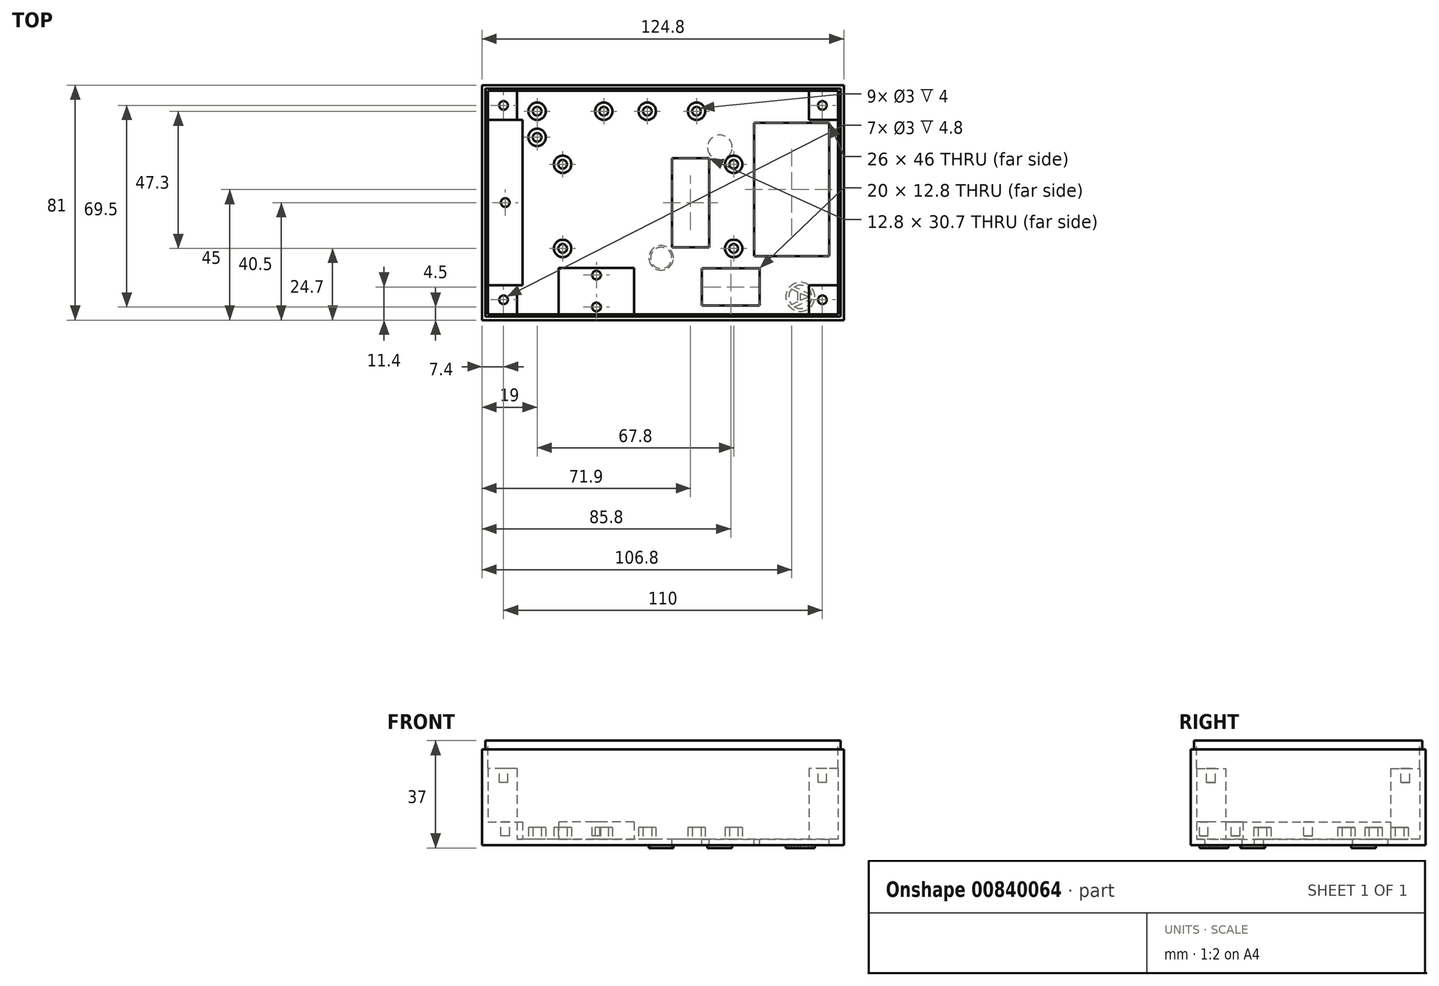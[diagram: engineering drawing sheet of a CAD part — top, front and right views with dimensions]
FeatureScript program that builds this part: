
annotation { "Feature Type Name" : "Feature", "Feature Type Description" : "" }
export const myFeature = defineFeature(function(context is Context, id is Id, definition is map)
    precondition{}
    {
        {
            var Q0;
            Q0=qCreatedBy(makeId("Top.planeOp"),FACE);
            var sketch = newSketch(context, id + "F0", { "sketchPlane" : qUnion([Q0])});
            skLineSegment(sketch, "E0.bottom", {"start": v(62.4, -40.5) * mm, "end": v(-62.4, -40.5) * mm});
            skLineSegment(sketch, "E0.top", {"start": v(62.4, 40.5) * mm, "end": v(-62.4, 40.5) * mm});
            skLineSegment(sketch, "E0.left", {"start": v(62.4, -40.5) * mm, "end": v(62.4, 40.5) * mm});
            skLineSegment(sketch, "E0.right", {"start": v(-62.4, -40.5) * mm, "end": v(-62.4, 40.5) * mm});
            skPoint(sketch, "E0.middle", {"position": v(0, 0) * mm});
            skSolve(sketch);
        }
        {
            var Q0;
            Q0=qSketchRegion(id+"F0",true);
            extrude(context, id + "F1", {"entities" : qUnion([Q0]), "depth" : 33 * mm, "offsetDistance" : 25 * mm});
        }
        {
            var Q0;
            Q0=makeQuery(id+"F1.opExtrude","CAP_FACE",FACE,{"disambiguationData":[OSD([sQuery(id+"F0.wireOp",EDGE,"E0.bottom"),sQuery(id+"F0.wireOp",EDGE,"E0.top"),sQuery(id+"F0.wireOp",EDGE,"E0.left"),sQuery(id+"F0.wireOp",EDGE,"E0.right")])],"isStart":false});
            var sketch = newSketch(context, id + "F2", { "sketchPlane" : qUnion([Q0])});
            skLineSegment(sketch, "E1.bottom", {"start": v(61.25, -39.35) * mm, "end": v(-61.25, -39.35) * mm});
            skLineSegment(sketch, "E1.top", {"start": v(61.25, 39.35) * mm, "end": v(-61.25, 39.35) * mm});
            skLineSegment(sketch, "E1.left", {"start": v(61.25, -39.35) * mm, "end": v(61.25, 39.35) * mm});
            skLineSegment(sketch, "E1.right", {"start": v(-61.25, -39.35) * mm, "end": v(-61.25, 39.35) * mm});
            skPoint(sketch, "E1.middle", {"position": v(0, 0) * mm});
            skSolve(sketch);
        }
        {
            var Q0;
            Q0=qSketchRegion(id+"F2",true);
            extrude(context, id + "F3", {"entities" : qUnion([Q0]), "operationType" : NewBodyOperationType.ADD, "depth" : 3 * mm, "offsetDistance" : 25 * mm});
        }
        {
            var Q0;
            Q0=makeQuery(id+"F3.opExtrude","CAP_FACE",FACE,{"disambiguationData":[OSD([sQuery(id+"F2.wireOp",EDGE,"E1.bottom"),sQuery(id+"F2.wireOp",EDGE,"E1.top"),sQuery(id+"F2.wireOp",EDGE,"E1.left"),sQuery(id+"F2.wireOp",EDGE,"E1.right")])],"isStart":false});
            var sketch = newSketch(context, id + "F4", { "sketchPlane" : qUnion([Q0])});
            skLineSegment(sketch, "E2.bottom", {"start": v(60.4, -38.5) * mm, "end": v(-60.4, -38.5) * mm});
            skLineSegment(sketch, "E2.top", {"start": v(60.4, 38.5) * mm, "end": v(-60.4, 38.5) * mm});
            skLineSegment(sketch, "E2.left", {"start": v(60.4, -38.5) * mm, "end": v(60.4, 38.5) * mm});
            skLineSegment(sketch, "E2.right", {"start": v(-60.4, -38.5) * mm, "end": v(-60.4, 38.5) * mm});
            skPoint(sketch, "E2.middle", {"position": v(0, 0) * mm});
            skSolve(sketch);
        }
        {
            var Q0;
            Q0=qSketchRegion(id+"F4",true);
            extrude(context, id + "F5", {"entities" : qUnion([Q0]), "operationType" : NewBodyOperationType.REMOVE, "oppositeDirection" : true, "depth" : 34 * mm, "offsetDistance" : 25 * mm});
        }
        {
            var Q0;
            Q0=makeQuery(id+"F5.boolean.opBoolean","COPY",FACE,{"derivedFrom":makeQuery(id+"F5.opExtrude","CAP_FACE",FACE,{"disambiguationData":[OSD([sQuery(id+"F4.wireOp",EDGE,"E2.bottom"),sQuery(id+"F4.wireOp",EDGE,"E2.top"),sQuery(id+"F4.wireOp",EDGE,"E2.left"),sQuery(id+"F4.wireOp",EDGE,"E2.right")])],"isStart":false})});
            var sketch = newSketch(context, id + "F6", { "sketchPlane" : qUnion([Q0])});
            skLineSegment(sketch, "E3.bottom", {"start": v(-60.4, 38.5) * mm, "end": v(-50.4, 38.5) * mm});
            skLineSegment(sketch, "E3.top", {"start": v(-60.4, 28.5) * mm, "end": v(-50.4, 28.5) * mm});
            skLineSegment(sketch, "E3.left", {"start": v(-60.4, 38.5) * mm, "end": v(-60.4, 28.5) * mm});
            skLineSegment(sketch, "E3.right", {"start": v(-50.4, 38.5) * mm, "end": v(-50.4, 28.5) * mm});
            skLineSegment(sketch, "E4.bottom", {"start": v(-60.4, -38.5) * mm, "end": v(-50.4, -38.5) * mm});
            skLineSegment(sketch, "E4.top", {"start": v(-60.4, -28.5) * mm, "end": v(-50.4, -28.5) * mm});
            skLineSegment(sketch, "E4.left", {"start": v(-60.4, -38.5) * mm, "end": v(-60.4, -28.5) * mm});
            skLineSegment(sketch, "E4.right", {"start": v(-50.4, -38.5) * mm, "end": v(-50.4, -28.5) * mm});
            skLineSegment(sketch, "E5.bottom", {"start": v(60.4, -38.5) * mm, "end": v(50.4, -38.5) * mm});
            skLineSegment(sketch, "E5.top", {"start": v(60.4, -28.5) * mm, "end": v(50.4, -28.5) * mm});
            skLineSegment(sketch, "E5.left", {"start": v(60.4, -38.5) * mm, "end": v(60.4, -28.5) * mm});
            skLineSegment(sketch, "E5.right", {"start": v(50.4, -38.5) * mm, "end": v(50.4, -28.5) * mm});
            skLineSegment(sketch, "E6.bottom", {"start": v(60.4, 38.5) * mm, "end": v(50.4, 38.5) * mm});
            skLineSegment(sketch, "E6.top", {"start": v(60.4, 28.5) * mm, "end": v(50.4, 28.5) * mm});
            skLineSegment(sketch, "E6.left", {"start": v(60.4, 38.5) * mm, "end": v(60.4, 28.5) * mm});
            skLineSegment(sketch, "E6.right", {"start": v(50.4, 38.5) * mm, "end": v(50.4, 28.5) * mm});
            skSolve(sketch);
        }
        {
            var Q0;
            Q0=qSketchRegion(id+"F6",true);
            extrude(context, id + "F7", {"entities" : qUnion([Q0]), "operationType" : NewBodyOperationType.ADD, "depth" : 24.4 * mm, "offsetDistance" : 25 * mm});
        }
        {
            var Q0;
            Q0=makeQuery(id+"F7.opExtrude","CAP_FACE",FACE,{"disambiguationData":[OSD([sQuery(id+"F6.wireOp",EDGE,"E3.bottom"),sQuery(id+"F6.wireOp",EDGE,"E3.top"),sQuery(id+"F6.wireOp",EDGE,"E3.left"),sQuery(id+"F6.wireOp",EDGE,"E3.right")])],"isStart":false});
            var sketch = newSketch(context, id + "F8", { "sketchPlane" : qUnion([Q0])});
            skCircle(sketch, "E7", {"center": v(-55, 33.5) * mm, "radius": 1.5 * mm});
            skPoint(sketch, "E7.centerSnap0", {"position": v(-50.4, 33.5) * mm});
            skCircle(sketch, "E8", {"center": v(-55, -33.5) * mm, "radius": 1.5 * mm});
            skCircle(sketch, "E9", {"center": v(55, -33.5) * mm, "radius": 1.5 * mm});
            skCircle(sketch, "E10", {"center": v(55, 33.5) * mm, "radius": 1.5 * mm});
            skSolve(sketch);
        }
        {
            var Q0;
            Q0=qSketchRegion(id+"F8",true);
            extrude(context, id + "F9", {"entities" : qUnion([Q0]), "operationType" : NewBodyOperationType.REMOVE, "oppositeDirection" : true, "depth" : 4.8 * mm, "offsetDistance" : 25 * mm});
        }
        {
            var Q0;
            Q0=makeQuery(id+"F5.boolean.opBoolean","COPY",FACE,{"derivedFrom":makeQuery(id+"F5.opExtrude","CAP_FACE",FACE,{"disambiguationData":[OSD([sQuery(id+"F4.wireOp",EDGE,"E2.bottom"),sQuery(id+"F4.wireOp",EDGE,"E2.top"),sQuery(id+"F4.wireOp",EDGE,"E2.left"),sQuery(id+"F4.wireOp",EDGE,"E2.right")])],"isStart":false})});
            var sketch = newSketch(context, id + "F10", { "sketchPlane" : qUnion([Q0])});
            skLineSegment(sketch, "E11.bottom", {"start": v(31.4, 27.5) * mm, "end": v(57.4, 27.5) * mm});
            skLineSegment(sketch, "E11.top", {"start": v(31.4, -18.5) * mm, "end": v(57.4, -18.5) * mm});
            skLineSegment(sketch, "E11.left", {"start": v(31.4, 27.5) * mm, "end": v(31.4, -18.5) * mm});
            skLineSegment(sketch, "E11.right", {"start": v(57.4, 27.5) * mm, "end": v(57.4, -18.5) * mm});
            skLineSegment(sketch, "E12.bottom", {"start": v(13.4, -22.7) * mm, "end": v(33.4, -22.7) * mm});
            skLineSegment(sketch, "E12.top", {"start": v(13.4, -35.5) * mm, "end": v(33.4, -35.5) * mm});
            skLineSegment(sketch, "E12.left", {"start": v(13.4, -22.7) * mm, "end": v(13.4, -35.5) * mm});
            skLineSegment(sketch, "E12.right", {"start": v(33.4, -22.7) * mm, "end": v(33.4, -35.5) * mm});
            skLineSegment(sketch, "E13.bottom", {"start": v(15.9, -15.35) * mm, "end": v(3.1, -15.35) * mm});
            skLineSegment(sketch, "E13.top", {"start": v(15.9, 15.35) * mm, "end": v(3.1, 15.35) * mm});
            skLineSegment(sketch, "E13.left", {"start": v(15.9, -15.35) * mm, "end": v(15.9, 15.35) * mm});
            skLineSegment(sketch, "E13.right", {"start": v(3.1, -15.35) * mm, "end": v(3.1, 15.35) * mm});
            skPoint(sketch, "E13.middle", {"position": v(9.5, 0) * mm});
            skSolve(sketch);
        }
        {
            var Q0;
            Q0=qSketchRegion(id+"F10",true);
            extrude(context, id + "F11", {"entities" : qUnion([Q0]), "operationType" : NewBodyOperationType.REMOVE, "endBound" : BoundingType.THROUGH_ALL, "oppositeDirection" : true, "depth" : 25 * mm, "offsetDistance" : 25 * mm});
        }
        {
            var Q0;
            Q0=makeQuery(id+"F5.boolean.opBoolean","COPY",FACE,{"derivedFrom":makeQuery(id+"F5.opExtrude","CAP_FACE",FACE,{"disambiguationData":[OSD([sQuery(id+"F4.wireOp",EDGE,"E2.bottom"),sQuery(id+"F4.wireOp",EDGE,"E2.top"),sQuery(id+"F4.wireOp",EDGE,"E2.left"),sQuery(id+"F4.wireOp",EDGE,"E2.right")])],"isStart":false})});
            var sketch = newSketch(context, id + "F12", { "sketchPlane" : qUnion([Q0])});
            skCircle(sketch, "E14", {"center": v(24.4, 13.2) * mm, "radius": 3 * mm});
            skCircle(sketch, "E15", {"center": v(-34.6, 13.2) * mm, "radius": 3 * mm});
            skCircle(sketch, "E16", {"center": v(-34.6, -15.8) * mm, "radius": 3 * mm});
            skCircle(sketch, "E17", {"center": v(24.4, -15.8) * mm, "radius": 3 * mm});
            skCircle(sketch, "E18", {"center": v(-43.4, 31.5) * mm, "radius": 3 * mm});
            skCircle(sketch, "E19", {"center": v(-43.4, 22.5) * mm, "radius": 3 * mm});
            skCircle(sketch, "E20", {"center": v(-20.4, 31.5) * mm, "radius": 3 * mm});
            skCircle(sketch, "E21", {"center": v(-5.4, 31.5) * mm, "radius": 3 * mm});
            skCircle(sketch, "E22", {"center": v(11.6, 31.5) * mm, "radius": 3 * mm});
            skSolve(sketch);
        }
        {
            var Q0;
            Q0=qSketchRegion(id+"F12",true);
            extrude(context, id + "F13", {"entities" : qUnion([Q0]), "operationType" : NewBodyOperationType.ADD, "depth" : 4 * mm, "offsetDistance" : 25 * mm});
        }
        {
            var Q0;
            Q0=makeQuery(id+"F5.boolean.opBoolean","COPY",FACE,{"derivedFrom":makeQuery(id+"F5.opExtrude","CAP_FACE",FACE,{"disambiguationData":[OSD([sQuery(id+"F4.wireOp",EDGE,"E2.bottom"),sQuery(id+"F4.wireOp",EDGE,"E2.top"),sQuery(id+"F4.wireOp",EDGE,"E2.left"),sQuery(id+"F4.wireOp",EDGE,"E2.right")])],"isStart":false})});
            var sketch = newSketch(context, id + "F14", { "sketchPlane" : qUnion([Q0])});
            skCircle(sketch, "E23", {"center": v(-34.6, -15.8) * mm, "radius": 1.5 * mm});
            skCircle(sketch, "E24", {"center": v(24.4, -15.8) * mm, "radius": 1.5 * mm});
            skCircle(sketch, "E25", {"center": v(-34.6, 13.2) * mm, "radius": 1.5 * mm});
            skCircle(sketch, "E26", {"center": v(24.4, 13.2) * mm, "radius": 1.5 * mm});
            skCircle(sketch, "E27", {"center": v(11.6, 31.5) * mm, "radius": 1.5 * mm});
            skCircle(sketch, "E28", {"center": v(-5.4, 31.5) * mm, "radius": 1.5 * mm});
            skCircle(sketch, "E29", {"center": v(-20.4, 31.5) * mm, "radius": 1.5 * mm});
            skCircle(sketch, "E30", {"center": v(-43.4, 22.5) * mm, "radius": 1.5 * mm});
            skCircle(sketch, "E31", {"center": v(-43.4, 31.5) * mm, "radius": 1.5 * mm});
            skSolve(sketch);
        }
        {
            var Q0;
            Q0=qSketchRegion(id+"F14",true);
            extrude(context, id + "F15", {"entities" : qUnion([Q0]), "operationType" : NewBodyOperationType.REMOVE, "depth" : 4.8 * mm, "offsetDistance" : 25 * mm});
        }
        {
            var Q0;
            Q0=makeQuery(id+"F5.boolean.opBoolean","COPY",FACE,{"derivedFrom":makeQuery(id+"F5.opExtrude","CAP_FACE",FACE,{"disambiguationData":[OSD([sQuery(id+"F4.wireOp",EDGE,"E2.bottom"),sQuery(id+"F4.wireOp",EDGE,"E2.top"),sQuery(id+"F4.wireOp",EDGE,"E2.left"),sQuery(id+"F4.wireOp",EDGE,"E2.right")])],"isStart":false})});
            var sketch = newSketch(context, id + "F16", { "sketchPlane" : qUnion([Q0])});
            skLineSegment(sketch, "E32.bottom", {"start": v(-60.4, -28.5) * mm, "end": v(-48.4, -28.5) * mm});
            skLineSegment(sketch, "E32.top", {"start": v(-60.4, 28.5) * mm, "end": v(-48.4, 28.5) * mm});
            skLineSegment(sketch, "E32.left", {"start": v(-60.4, -28.5) * mm, "end": v(-60.4, 28.5) * mm});
            skLineSegment(sketch, "E32.right", {"start": v(-48.4, -28.5) * mm, "end": v(-48.4, 28.5) * mm});
            skSolve(sketch);
        }
        {
            var Q0;
            Q0=qSketchRegion(id+"F16",true);
            extrude(context, id + "F17", {"entities" : qUnion([Q0]), "operationType" : NewBodyOperationType.ADD, "depth" : 6 * mm, "offsetDistance" : 25 * mm});
        }
        {
            var Q0;
            Q0=makeQuery(id+"F17.opExtrude","CAP_FACE",FACE,{"disambiguationData":[OSD([sQuery(id+"F16.wireOp",EDGE,"E32.bottom"),sQuery(id+"F16.wireOp",EDGE,"E32.top"),sQuery(id+"F16.wireOp",EDGE,"E32.left"),sQuery(id+"F16.wireOp",EDGE,"E32.right")])],"isStart":false});
            var sketch = newSketch(context, id + "F18", { "sketchPlane" : qUnion([Q0])});
            skCircle(sketch, "E33", {"center": v(-54.4, 0) * mm, "radius": 1.5 * mm});
            skPoint(sketch, "E33.centerSnap0", {"position": v(-48.4, 0) * mm});
            skSolve(sketch);
        }
        {
            var Q0;
            Q0=qSketchRegion(id+"F18",true);
            extrude(context, id + "F19", {"entities" : qUnion([Q0]), "operationType" : NewBodyOperationType.REMOVE, "oppositeDirection" : true, "depth" : 4.8 * mm, "offsetDistance" : 25 * mm});
        }
        {
            var Q0;
            Q0=makeQuery(id+"F5.boolean.opBoolean","COPY",FACE,{"derivedFrom":makeQuery(id+"F5.opExtrude","CAP_FACE",FACE,{"disambiguationData":[OSD([sQuery(id+"F4.wireOp",EDGE,"E2.bottom"),sQuery(id+"F4.wireOp",EDGE,"E2.top"),sQuery(id+"F4.wireOp",EDGE,"E2.left"),sQuery(id+"F4.wireOp",EDGE,"E2.right")])],"isStart":false})});
            var sketch = newSketch(context, id + "F20", { "sketchPlane" : qUnion([Q0])});
            skLineSegment(sketch, "E34.bottom", {"start": v(-35.93, -22.5) * mm, "end": v(-9.93, -22.5) * mm});
            skLineSegment(sketch, "E34.top", {"start": v(-35.93, -38.5) * mm, "end": v(-9.93, -38.5) * mm});
            skLineSegment(sketch, "E34.left", {"start": v(-35.93, -22.5) * mm, "end": v(-35.93, -38.5) * mm});
            skLineSegment(sketch, "E34.right", {"start": v(-9.93, -22.5) * mm, "end": v(-9.93, -38.5) * mm});
            skSolve(sketch);
        }
        {
            var Q0;
            Q0=qSketchRegion(id+"F20",true);
            extrude(context, id + "F21", {"entities" : qUnion([Q0]), "operationType" : NewBodyOperationType.ADD, "depth" : 6 * mm, "offsetDistance" : 25 * mm});
        }
        {
            var Q0;
            Q0=makeQuery(id+"F21.opExtrude","CAP_FACE",FACE,{"disambiguationData":[OSD([sQuery(id+"F20.wireOp",EDGE,"E34.bottom"),sQuery(id+"F20.wireOp",EDGE,"E34.top"),sQuery(id+"F20.wireOp",EDGE,"E34.left"),sQuery(id+"F20.wireOp",EDGE,"E34.right")])],"isStart":false});
            var sketch = newSketch(context, id + "F22", { "sketchPlane" : qUnion([Q0])});
            skCircle(sketch, "E35", {"center": v(-22.93, -25) * mm, "radius": 1.5 * mm});
            skPoint(sketch, "E35.centerSnap0", {"position": v(-22.93, -22.5) * mm});
            skPoint(sketch, "E35.perimeterSnap0", {"position": v(-22.93, -22.5) * mm});
            skPoint(sketch, "E35.perimeterSnap1", {"position": v(-35.93, -30.5) * mm});
            skCircle(sketch, "E36", {"center": v(-22.93, -36) * mm, "radius": 1.5 * mm});
            skSolve(sketch);
        }
        {
            var Q0;
            Q0=qSketchRegion(id+"F22",true);
            extrude(context, id + "F23", {"entities" : qUnion([Q0]), "operationType" : NewBodyOperationType.REMOVE, "oppositeDirection" : true, "depth" : 4.8 * mm, "offsetDistance" : 25 * mm});
        }
        {
            var Q0;
            Q0=makeQuery(id+"F1.opExtrude","CAP_FACE",FACE,{"disambiguationData":[OSD([sQuery(id+"F0.wireOp",EDGE,"E0.bottom"),sQuery(id+"F0.wireOp",EDGE,"E0.top"),sQuery(id+"F0.wireOp",EDGE,"E0.left"),sQuery(id+"F0.wireOp",EDGE,"E0.right")])],"isStart":true});
            var sketch = newSketch(context, id + "F24", { "sketchPlane" : qUnion([Q0])});
            skCircle(sketch, "E37", {"center": v(47.4, 32.5) * mm, "radius": 5 * mm});
            skCircle(sketch, "E38", {"center": v(47.4, 32.5) * mm, "radius": 4 * mm});
            skSolve(sketch);
        }
        {
            var Q0;
            Q0=qSketchRegion(id+"F24",true);
            extrude(context, id + "F25", {"entities" : qUnion([Q0]), "operationType" : NewBodyOperationType.ADD, "depth" : 1 * mm, "offsetDistance" : 25 * mm});
        }
        {
            var Q0;
            {var subQ12=sQuery(id+"F0.wireOp",EDGE,"E0.right");var subQ14=sQuery(id+"F0.wireOp",EDGE,"E0.top");var subQ16=sQuery(id+"F0.wireOp",EDGE,"E0.left");var subQ18=sQuery(id+"F0.wireOp",EDGE,"E0.bottom");var subQ19=makeQuery(id+"F1.opExtrude","SWEPT_FACE",FACE,{"disambiguationData":[OSD([subQ18])]});Q0=makeQuery(id+"FWEkfTlQKALJ9jg_1.boolean.opBoolean","SPLIT",FACE,{"disambiguationData":[TD([subQ19])],"derivedFrom":makeQuery(id+"F25.boolean.opBoolean","SPLIT",FACE,{"disambiguationData":[TD([subQ19])],"derivedFrom":makeQuery(id+"F1.opExtrude","CAP_FACE",FACE,{"disambiguationData":[OSD([subQ18,subQ14,subQ16,subQ12])],"isStart":true})})});}
            var sketch = newSketch(context, id + "F26", { "sketchPlane" : qUnion([Q0])});
            skLineSegment(sketch, "E39", {"start": v(44.91, 36.12) * mm, "end": v(51.52, 33.06) * mm});
            skLineSegment(sketch, "E40", {"start": v(51.52, 33.06) * mm, "end": v(51.52, 31.97) * mm});
            skLineSegment(sketch, "E41", {"start": v(51.52, 31.97) * mm, "end": v(45.1, 28.97) * mm});
            skLineSegment(sketch, "E42", {"start": v(45.1, 28.97) * mm, "end": v(44.19, 29.7) * mm});
            skLineSegment(sketch, "E43", {"start": v(44.19, 29.7) * mm, "end": v(46.4, 30.75) * mm});
            skLineSegment(sketch, "E44", {"start": v(46.4, 30.75) * mm, "end": v(46.4, 34.26) * mm});
            skLineSegment(sketch, "E45", {"start": v(46.4, 34.26) * mm, "end": v(44.17, 35.3) * mm});
            skLineSegment(sketch, "E46", {"start": v(44.17, 35.3) * mm, "end": v(44.91, 36.12) * mm});
            skLineSegment(sketch, "E47", {"start": v(50.23, 32.5) * mm, "end": v(47.48, 33.76) * mm});
            skLineSegment(sketch, "E48", {"start": v(47.48, 33.76) * mm, "end": v(47.48, 31.24) * mm});
            skLineSegment(sketch, "E49", {"start": v(47.48, 31.24) * mm, "end": v(50.23, 32.5) * mm});
            skSolve(sketch);
        }
        {
            var Q0;
            Q0=makeQuery(id+"F26.imprint","IMPRINT",FACE,{"disambiguationData":[TD([[makeQuery(id+"F26.imprint","IMPRINT",EDGE,{"derivedFrom":sQuery(id+"F26.wireOp",EDGE,"E39")}),-1.0]])]});
            extrude(context, id + "F27", {"entities" : qUnion([Q0]), "operationType" : NewBodyOperationType.ADD, "depth" : 1 * mm, "offsetDistance" : 25 * mm});
        }
        {
            var Q0;
            {var subQ12=sQuery(id+"F0.wireOp",EDGE,"E0.right");var subQ14=sQuery(id+"F0.wireOp",EDGE,"E0.top");var subQ16=sQuery(id+"F0.wireOp",EDGE,"E0.left");var subQ18=sQuery(id+"F0.wireOp",EDGE,"E0.bottom");var subQ19=makeQuery(id+"F1.opExtrude","SWEPT_FACE",FACE,{"disambiguationData":[OSD([subQ18])]});Q0=makeQuery(id+"FWEkfTlQKALJ9jg_1.boolean.opBoolean","SPLIT",FACE,{"disambiguationData":[TD([subQ19])],"derivedFrom":makeQuery(id+"F25.boolean.opBoolean","SPLIT",FACE,{"disambiguationData":[TD([subQ19])],"derivedFrom":makeQuery(id+"F1.opExtrude","CAP_FACE",FACE,{"disambiguationData":[OSD([subQ18,subQ14,subQ16,subQ12])],"isStart":true})})});}
            var sketch = newSketch(context, id + "F28", { "sketchPlane" : qUnion([Q0])});
            skCircle(sketch, "E50", {"center": v(19.61, -19.06) * mm, "radius": 4.25 * mm});
            skCircle(sketch, "E51", {"center": v(-0.61, 19.06) * mm, "radius": 4.25 * mm});
            skLineSegment(sketch, "E52", {"start": v(15.9, -15.35) * mm, "end": v(19.61, -19.06) * mm, "construction": true});
            skLineSegment(sketch, "E53", {"start": v(3.1, 15.35) * mm, "end": v(-0.61, 19.06) * mm, "construction": true});
            skCircle(sketch, "E54", {"center": v(-0.61, 19.06) * mm, "radius": 3.65 * mm});
            skSolve(sketch);
        }
        {
            var Q0;
            Q0=qSketchRegion(id+"F28",true);
            extrude(context, id + "F29", {"entities" : qUnion([Q0]), "operationType" : NewBodyOperationType.ADD, "depth" : 1 * mm, "offsetDistance" : 25 * mm});
        }
    });
